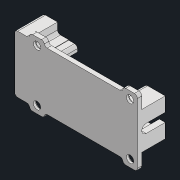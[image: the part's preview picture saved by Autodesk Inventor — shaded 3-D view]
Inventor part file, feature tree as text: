
AUTODESK INVENTOR PART (.ipt)
format: ipt  version: 2022.2 (Build 262287010, 287A)  size: 276,480 bytes
history: native  units: mm
features: reference x8, extrude x5, sketch x4, other x3, chamfer x1, mirror x1, fillet x1
ambient origin geometry x8: Origin, YZ Plane, XZ Plane, XY Plane, X Axis, Y Axis, Z Axis, Center Point
bodies: Solid1 (feature_tree)
feature tree (23):
  extrude  "Extrusion1"  Depth=3.0mm TaperAngle=0.0deg
  extrude  "Extrusion2"  Depth=2.0mm
  chamfer  "Chamfer4"  Distance=2.0mm Angle=45.0deg
  mirror  "Mirror1"
  extrude  "Extrusion8"  Depth=3.0mm
  extrude  "Extrusion9"  TaperAngle=0.0deg  [1 undecoded]
  extrude  "Extrusion10"  Depth=10.0mm
  fillet  "Fillet2"  Radius=0.25mm
  sketch  "Sketch2"  dims[d16=0.0mm d17=3.0mm d18=0.0mm]
  reference  "Reference12"
  reference  "Reference13"
  reference  "Reference14"
  reference  "Reference15"
  reference  "Reference16"
  reference  "Reference17"
  reference  "Reference18"
  reference  "Reference21"
  sketch  "Sketch8"  dims[d60=10.0mm d70=2.0mm]
  sketch  "Sketch9"  dims[d73=5.0mm]
  sketch  "Sketch11"  dims[d74=1.5mm d75=2.0mm d76=45.0deg d78=3.0mm d79=0.0mm d80=0.25mm d81=0.25mm d82=3.0mm d83=0.0mm d84=0.25mm d85=10.0mm d86=10.0mm d87=0.0mm d88=0.0mm d54=0.5mm d55=0.872665mm d56=0.5mm d57=0.872665mm]
  parser-record x1  (decoder bookkeeping rows leaked as tree rows — omitted from the tree; the rows remain in map.json)
  other  "Assembly1.iam"
  other  "Syringe:1"
note: 1 required parameter value undecoded (feature->parameter linkage not recoverable at this tier; creation-order binding heuristic only, values carry confidence <= 0.55)
note: 1 file-system path scrubbed to <path> (originals preserved in map.json)
